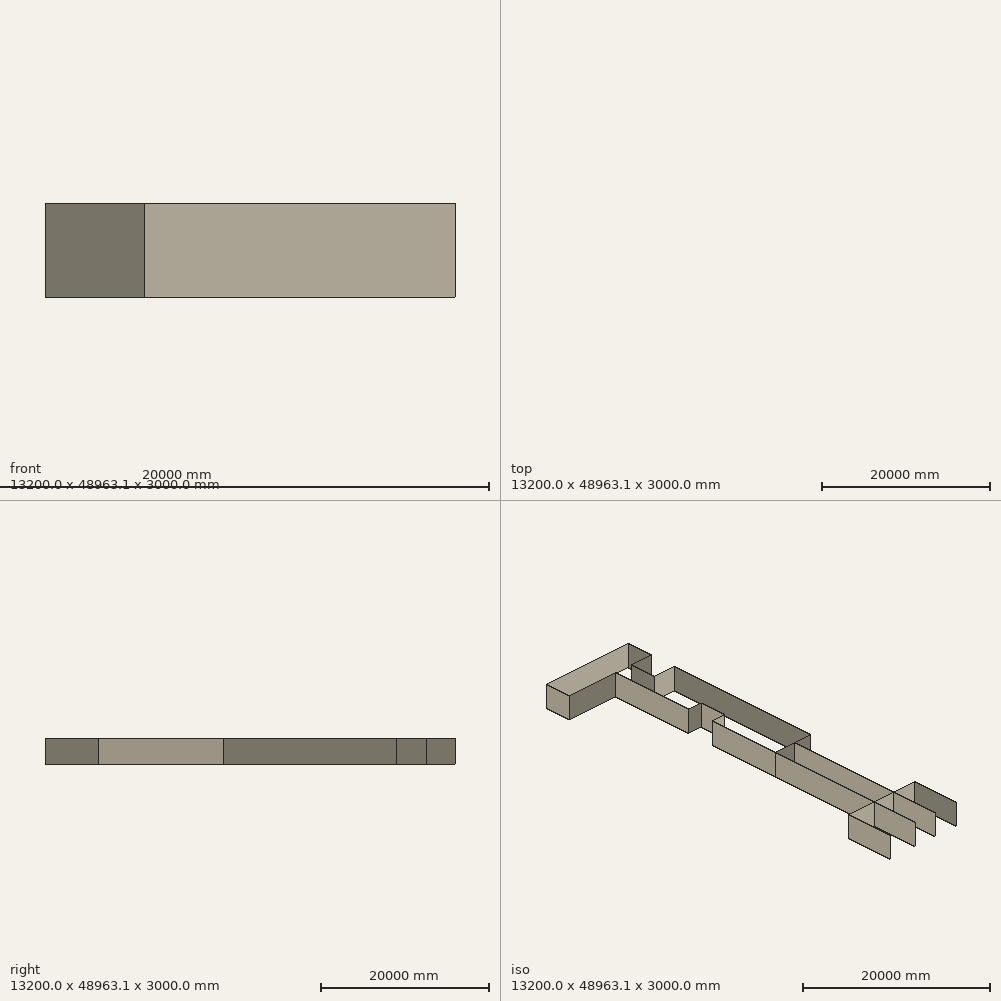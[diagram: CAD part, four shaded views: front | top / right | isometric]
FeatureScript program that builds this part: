
annotation { "Feature Type Name" : "Feature", "Feature Type Description" : "" }
export const myFeature = defineFeature(function(context is Context, id is Id, definition is map)
    precondition{}
    {
        {
            var Q0;
            Q0=qCreatedBy(makeId("Top.planeOp"),FACE);
            var sketch = newSketch(context, id + "F0", { "sketchPlane" : qUnion([Q0])});
            skLineSegment(sketch, "E0.bottom", {"start": v(0, 0) * mm, "end": v(20000, 0) * mm});
            skLineSegment(sketch, "E0.top", {"start": v(0, 50000) * mm, "end": v(20000, 50000) * mm});
            skLineSegment(sketch, "E0.left", {"start": v(0, 0) * mm, "end": v(0, 50000) * mm});
            skLineSegment(sketch, "E0.right", {"start": v(20000, 0) * mm, "end": v(20000, 50000) * mm});
            skSolve(sketch);
        }
        {
            var Q0;
            Q0=makeQuery(id+"F0.imprint","IMPRINT",FACE,{"disambiguationData":[TD([[makeQuery(id+"F0.imprint","IMPRINT",EDGE,{"derivedFrom":sQuery(id+"F0.wireOp",EDGE,"E0.bottom")}),1.0]])]});
            var sketch = newSketch(context, id + "F1", { "sketchPlane" : qUnion([Q0])});
            skLineSegment(sketch, "E1.bottom", {"start": v(0, 0) * mm, "end": v(9500, 0) * mm});
            skLineSegment(sketch, "E1.top", {"start": v(0, 6300) * mm, "end": v(9500, 6300) * mm});
            skLineSegment(sketch, "E1.left", {"start": v(0, 0) * mm, "end": v(0, 6300) * mm});
            skLineSegment(sketch, "E1.right", {"start": v(9500, 0) * mm, "end": v(9500, 6300) * mm});
            skSolve(sketch);
        }
        {
            var Q0;
            Q0=makeQuery(id+"F0.imprint","IMPRINT",FACE,{"disambiguationData":[TD([[makeQuery(id+"F0.imprint","IMPRINT",EDGE,{"derivedFrom":sQuery(id+"F0.wireOp",EDGE,"E0.bottom")}),1.0]])]});
            var sketch = newSketch(context, id + "F2", { "sketchPlane" : qUnion([Q0])});
            skLineSegment(sketch, "E2.bottom", {"start": v(10000, 0) * mm, "end": v(20000, 0) * mm});
            skLineSegment(sketch, "E2.top", {"start": v(10000, 6300) * mm, "end": v(20000, 6300) * mm});
            skLineSegment(sketch, "E2.left", {"start": v(10000, 0) * mm, "end": v(10000, 6300) * mm});
            skLineSegment(sketch, "E2.right", {"start": v(20000, 0) * mm, "end": v(20000, 6300) * mm});
            skSolve(sketch);
        }
        {
            var Q0;
            Q0=makeQuery(id+"F0.imprint","IMPRINT",FACE,{"disambiguationData":[TD([[makeQuery(id+"F0.imprint","IMPRINT",EDGE,{"derivedFrom":sQuery(id+"F0.wireOp",EDGE,"E0.bottom")}),1.0]])]});
            var sketch = newSketch(context, id + "F3", { "sketchPlane" : qUnion([Q0])});
            skLineSegment(sketch, "E3.bottom", {"start": v(13800, 0) * mm, "end": v(16800, 0) * mm});
            skLineSegment(sketch, "E3.top", {"start": v(13800, 6300) * mm, "end": v(16800, 6300) * mm});
            skLineSegment(sketch, "E3.left", {"start": v(13800, 0) * mm, "end": v(13800, 6300) * mm});
            skLineSegment(sketch, "E3.right", {"start": v(16800, 0) * mm, "end": v(16800, 6300) * mm});
            skSolve(sketch);
        }
        {
            var Q0;
            Q0=makeQuery(id+"F0.imprint","IMPRINT",FACE,{"disambiguationData":[TD([[makeQuery(id+"F0.imprint","IMPRINT",EDGE,{"derivedFrom":sQuery(id+"F0.wireOp",EDGE,"E0.bottom")}),1.0]])]});
            var sketch = newSketch(context, id + "F4", { "sketchPlane" : qUnion([Q0])});
            skLineSegment(sketch, "E4.bottom", {"start": v(13000, 9300) * mm, "end": v(2000, 9300) * mm});
            skLineSegment(sketch, "E4.top", {"start": v(13000, 21300) * mm, "end": v(2000, 21300) * mm});
            skLineSegment(sketch, "E4.left", {"start": v(13000, 9300) * mm, "end": v(13000, 21300) * mm});
            skLineSegment(sketch, "E4.right", {"start": v(2000, 9300) * mm, "end": v(2000, 21300) * mm});
            skSolve(sketch);
        }
        {
            var Q0;
            Q0=makeQuery(id+"F0.imprint","IMPRINT",FACE,{"disambiguationData":[TD([[makeQuery(id+"F0.imprint","IMPRINT",EDGE,{"derivedFrom":sQuery(id+"F0.wireOp",EDGE,"E0.bottom")}),1.0]])]});
            var sketch = newSketch(context, id + "F5", { "sketchPlane" : qUnion([Q0])});
            skLineSegment(sketch, "E5.bottom", {"start": v(16800, 6300) * mm, "end": v(13800, 6300) * mm});
            skLineSegment(sketch, "E5.top", {"start": v(16800, 21300) * mm, "end": v(13800, 21300) * mm});
            skLineSegment(sketch, "E5.left", {"start": v(16800, 6300) * mm, "end": v(16800, 21300) * mm});
            skLineSegment(sketch, "E5.right", {"start": v(13800, 6300) * mm, "end": v(13800, 21300) * mm});
            skSolve(sketch);
        }
        {
            var Q0;
            Q0=makeQuery(id+"F0.imprint","IMPRINT",FACE,{"disambiguationData":[TD([[makeQuery(id+"F0.imprint","IMPRINT",EDGE,{"derivedFrom":sQuery(id+"F0.wireOp",EDGE,"E0.bottom")}),1.0]])]});
            var sketch = newSketch(context, id + "F6", { "sketchPlane" : qUnion([Q0])});
            skLineSegment(sketch, "E6.bottom", {"start": v(19200, 21300) * mm, "end": v(13800, 21300) * mm});
            skLineSegment(sketch, "E6.top", {"start": v(19200, 48963.1) * mm, "end": v(13800, 48963.1) * mm});
            skLineSegment(sketch, "E6.left", {"start": v(19200, 21300) * mm, "end": v(19200, 48963.1) * mm});
            skLineSegment(sketch, "E6.right", {"start": v(13800, 21300) * mm, "end": v(13800, 48963.1) * mm});
            skSolve(sketch);
        }
        {
            var Q0;
            Q0=makeQuery(id+"F0.imprint","IMPRINT",FACE,{"disambiguationData":[TD([[makeQuery(id+"F0.imprint","IMPRINT",EDGE,{"derivedFrom":sQuery(id+"F0.wireOp",EDGE,"E0.bottom")}),1.0]])]});
            var sketch = newSketch(context, id + "F7", { "sketchPlane" : qUnion([Q0])});
            skLineSegment(sketch, "E7.bottom", {"start": v(13800, 48963.1) * mm, "end": v(6800, 48963.1) * mm});
            skLineSegment(sketch, "E7.top", {"start": v(13800, 45463.1) * mm, "end": v(6800, 45463.1) * mm});
            skLineSegment(sketch, "E7.left", {"start": v(13800, 48963.1) * mm, "end": v(13800, 45463.1) * mm});
            skLineSegment(sketch, "E7.right", {"start": v(6800, 48963.1) * mm, "end": v(6800, 45463.1) * mm});
            skSolve(sketch);
        }
        {
            var Q0;
            Q0=makeQuery(id+"F0.imprint","IMPRINT",FACE,{"disambiguationData":[TD([[makeQuery(id+"F0.imprint","IMPRINT",EDGE,{"derivedFrom":sQuery(id+"F0.wireOp",EDGE,"E0.bottom")}),1.0]])]});
            var sketch = newSketch(context, id + "F8", { "sketchPlane" : qUnion([Q0])});
            skLineSegment(sketch, "E8", {"start": v(0, 30000) * mm, "end": v(13492.73, 30000) * mm});
            skSolve(sketch);
        }
        {
            var Q0;
            Q0=makeQuery(id+"F0.imprint","IMPRINT",FACE,{"disambiguationData":[TD([[makeQuery(id+"F0.imprint","IMPRINT",EDGE,{"derivedFrom":sQuery(id+"F0.wireOp",EDGE,"E0.bottom")}),1.0]])]});
            var sketch = newSketch(context, id + "F9", { "sketchPlane" : qUnion([Q0])});
            skLineSegment(sketch, "E9.bottom", {"start": v(700, 34400) * mm, "end": v(15700, 34400) * mm});
            skLineSegment(sketch, "E9.top", {"start": v(700, 30800) * mm, "end": v(15700, 30800) * mm});
            skLineSegment(sketch, "E9.left", {"start": v(700, 34400) * mm, "end": v(700, 30800) * mm});
            skLineSegment(sketch, "E9.right", {"start": v(15700, 34400) * mm, "end": v(15700, 30800) * mm});
            skSolve(sketch);
        }
        {
            var Q0;
            Q0=makeQuery(id+"F0.imprint","IMPRINT",FACE,{"disambiguationData":[TD([[makeQuery(id+"F0.imprint","IMPRINT",EDGE,{"derivedFrom":sQuery(id+"F0.wireOp",EDGE,"E0.bottom")}),1.0]])]});
            var sketch = newSketch(context, id + "F10", { "sketchPlane" : qUnion([Q0])});
            skLineSegment(sketch, "E10.bottom", {"start": v(19200, 41963.1) * mm, "end": v(16200, 41963.1) * mm});
            skLineSegment(sketch, "E10.top", {"start": v(19200, 45463.1) * mm, "end": v(16200, 45463.1) * mm});
            skLineSegment(sketch, "E10.left", {"start": v(19200, 41963.1) * mm, "end": v(19200, 45463.1) * mm});
            skLineSegment(sketch, "E10.right", {"start": v(16200, 41963.1) * mm, "end": v(16200, 45463.1) * mm});
            skSolve(sketch);
        }
        {
            var Q0;
            Q0=makeQuery(id+"F0.imprint","IMPRINT",FACE,{"disambiguationData":[TD([[makeQuery(id+"F0.imprint","IMPRINT",EDGE,{"derivedFrom":sQuery(id+"F0.wireOp",EDGE,"E0.bottom")}),1.0]])]});
            var sketch = newSketch(context, id + "F11", { "sketchPlane" : qUnion([Q0])});
            skLineSegment(sketch, "E11.0", {"start": v(16800, 6300) * mm, "end": v(16800, 21300) * mm});
            skLineSegment(sketch, "E11.1", {"start": v(10000, 0) * mm, "end": v(10000, 6300) * mm});
            skLineSegment(sketch, "E11.2", {"start": v(10000, 6300) * mm, "end": v(20000, 6300) * mm});
            skLineSegment(sketch, "E11.3", {"start": v(13800, 6300) * mm, "end": v(13800, 21300) * mm});
            skLineSegment(sketch, "E11.4", {"start": v(13800, 0) * mm, "end": v(13800, 6300) * mm});
            skLineSegment(sketch, "E11.5", {"start": v(16800, 0) * mm, "end": v(16800, 6300) * mm});
            skLineSegment(sketch, "E11.6", {"start": v(16800, 21300) * mm, "end": v(13800, 21300) * mm});
            skLineSegment(sketch, "E11.7", {"start": v(19200, 21300) * mm, "end": v(13800, 21300) * mm});
            skLineSegment(sketch, "E11.8", {"start": v(19200, 21300) * mm, "end": v(19200, 41963.1) * mm});
            skLineSegment(sketch, "E11.9", {"start": v(19200, 48963.1) * mm, "end": v(13800, 48963.1) * mm});
            skLineSegment(sketch, "E11.10", {"start": v(13800, 48963.1) * mm, "end": v(6800, 48963.1) * mm});
            skLineSegment(sketch, "E11.11", {"start": v(6800, 48963.1) * mm, "end": v(6800, 45463.1) * mm});
            skLineSegment(sketch, "E11.12", {"start": v(13800, 45463.1) * mm, "end": v(6800, 45463.1) * mm});
            skLineSegment(sketch, "E11.14", {"start": v(13800, 21300) * mm, "end": v(13800, 30800) * mm});
            skLineSegment(sketch, "E11.15", {"start": v(16200, 41963.1) * mm, "end": v(16200, 45463.1) * mm});
            skLineSegment(sketch, "E11.16", {"start": v(19200, 41963.1) * mm, "end": v(16200, 41963.1) * mm});
            skLineSegment(sketch, "E11.17", {"start": v(19200, 45463.1) * mm, "end": v(16200, 45463.1) * mm});
            skLineSegment(sketch, "E11.18", {"start": v(13800, 30800) * mm, "end": v(15700, 30800) * mm});
            skLineSegment(sketch, "E11.19", {"start": v(15700, 34400) * mm, "end": v(15700, 30800) * mm});
            skLineSegment(sketch, "E11.20", {"start": v(13800, 34400) * mm, "end": v(15700, 34400) * mm});
            skLineSegment(sketch, "E11.22", {"start": v(20000, 0) * mm, "end": v(20000, 6300) * mm});
            skLineSegment(sketch, "E11.23", {"start": v(10000, 0) * mm, "end": v(20000, 0) * mm});
            skLineSegment(sketch, "E12.trimOffspring", {"start": v(19200, 45463.1) * mm, "end": v(19200, 48963.1) * mm});
            skPoint(sketch, "E11.13.start.orphan", {"position": v(13800, 48963.1) * mm});
            skLineSegment(sketch, "E13.trimOffspring", {"start": v(13800, 34400) * mm, "end": v(13800, 45463.1) * mm});
            skPoint(sketch, "E11.21.end.orphan", {"position": v(700, 30800) * mm});
            skPoint(sketch, "E11.21.start.orphan", {"position": v(700, 34400) * mm});
            skSolve(sketch);
        }
        {
            var Q0;
            Q0=sQuery(id+"F11.wireOp",EDGE,"E11.7");
            var Q1;
            Q1=sQuery(id+"F11.wireOp",EDGE,"E11.8");
            var Q2;
            Q2=sQuery(id+"F11.wireOp",EDGE,"E11.16");
            var Q3;
            Q3=sQuery(id+"F11.wireOp",EDGE,"E11.15");
            var Q4;
            Q4=sQuery(id+"F11.wireOp",EDGE,"E11.17");
            var Q5;
            Q5=sQuery(id+"F11.wireOp",EDGE,"E12.trimOffspring");
            var Q6;
            Q6=sQuery(id+"F11.wireOp",EDGE,"E11.9");
            var Q7;
            Q7=sQuery(id+"F11.wireOp",EDGE,"E11.10");
            var Q8;
            Q8=sQuery(id+"F11.wireOp",EDGE,"E11.11");
            var Q9;
            Q9=sQuery(id+"F11.wireOp",EDGE,"E11.12");
            var Q10;
            Q10=sQuery(id+"F11.wireOp",EDGE,"E13.trimOffspring");
            var Q11;
            Q11=sQuery(id+"F11.wireOp",EDGE,"E11.14");
            var Q12;
            Q12=sQuery(id+"F11.wireOp",EDGE,"E11.20");
            var Q13;
            Q13=sQuery(id+"F11.wireOp",EDGE,"E11.19");
            var Q14;
            Q14=sQuery(id+"F11.wireOp",EDGE,"E11.18");
            extrude(context, id + "F12", {"bodyType" : ToolBodyType.SURFACE, "surfaceEntities" : qUnion([Q0, Q1, Q2, Q3, Q4, Q5, Q6, Q7, Q8, Q9, Q10, Q11, Q12, Q13, Q14]), "depth" : 3000 * mm});
        }
        {
            var Q0;
            Q0=sQuery(id+"F11.wireOp",EDGE,"E11.3");
            var Q1;
            Q1=sQuery(id+"F11.wireOp",EDGE,"E11.0");
            extrude(context, id + "F13", {"bodyType" : ToolBodyType.SURFACE, "surfaceEntities" : qUnion([Q0, Q1]), "depth" : 3000 * mm});
        }
        {
            var Q0;
            Q0=sQuery(id+"F2.wireOp",EDGE,"E2.top");
            var Q1;
            Q1=sQuery(id+"F2.wireOp",EDGE,"E2.left");
            var Q2;
            Q2=sQuery(id+"F11.wireOp",EDGE,"E11.22");
            extrude(context, id + "F14", {"bodyType" : ToolBodyType.SURFACE, "surfaceEntities" : qUnion([Q0, Q1, Q2]), "depth" : 3000 * mm});
        }
        {
            var Q0;
            Q0=sQuery(id+"F11.wireOp",EDGE,"E11.4");
            var Q1;
            Q1=sQuery(id+"F11.wireOp",EDGE,"E11.5");
            extrude(context, id + "F15", {"bodyType" : ToolBodyType.SURFACE, "surfaceEntities" : qUnion([Q0, Q1]), "depth" : 3000 * mm});
        }
    });
